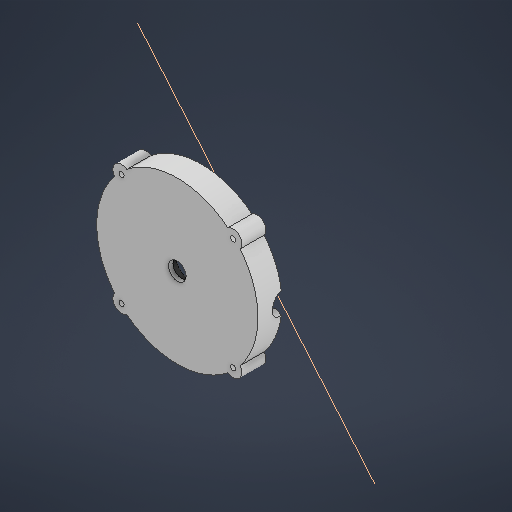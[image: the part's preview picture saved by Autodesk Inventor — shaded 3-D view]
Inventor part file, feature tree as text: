
AUTODESK INVENTOR PART (.ipt)
format: ipt  version: 2025.3 (Build 293356030, 356C)  size: 268,800 bytes
history: native  units: mm
features: sketch x5, extrude x4, plane x2, other x1
ambient origin geometry x8: Origin, YZ Plane, XZ Plane, XY Plane, X Axis, Y Axis, Z Axis, Center Point
bodies: Solid1 (feature_tree)
feature tree (12):
  sketch  "Sketch1"  dims[d1=40.0mm]
  extrude  "Extrusion1"  Depth=10.0mm TaperAngle=0.0deg
  extrude  "Extrusion2"  Depth=13.75mm TaperAngle=0.0deg
  extrude  "Extrusion3"  Depth=10.0mm
  sketch  "Sketch2"  dims[d12=7.5mm d13=0.0mm d14=13.75mm d15=0.0mm]
  plane  "Work Plane1"
  sketch  "Sketch3"  dims[d16=-13.089969mm d21=10.0mm]
  plane  "Work Plane3"
  extrude  "Extrusion5"  Depth=10.65mm
  other  "Work Axis1"
  sketch  "Sketch Circular Pattern1"  dims[d2=10.0mm d3=16.9mm d4=85.0mm d5=90.0mm d6=2.9mm d7=5.0mm d8=360.0deg d9=92.0mm d10=2.5mm d11=0.0mm]
  sketch  "Sketch5"  dims[d22=30.0deg d23=10.65mm d24=20.0mm d25=0.0mm]
